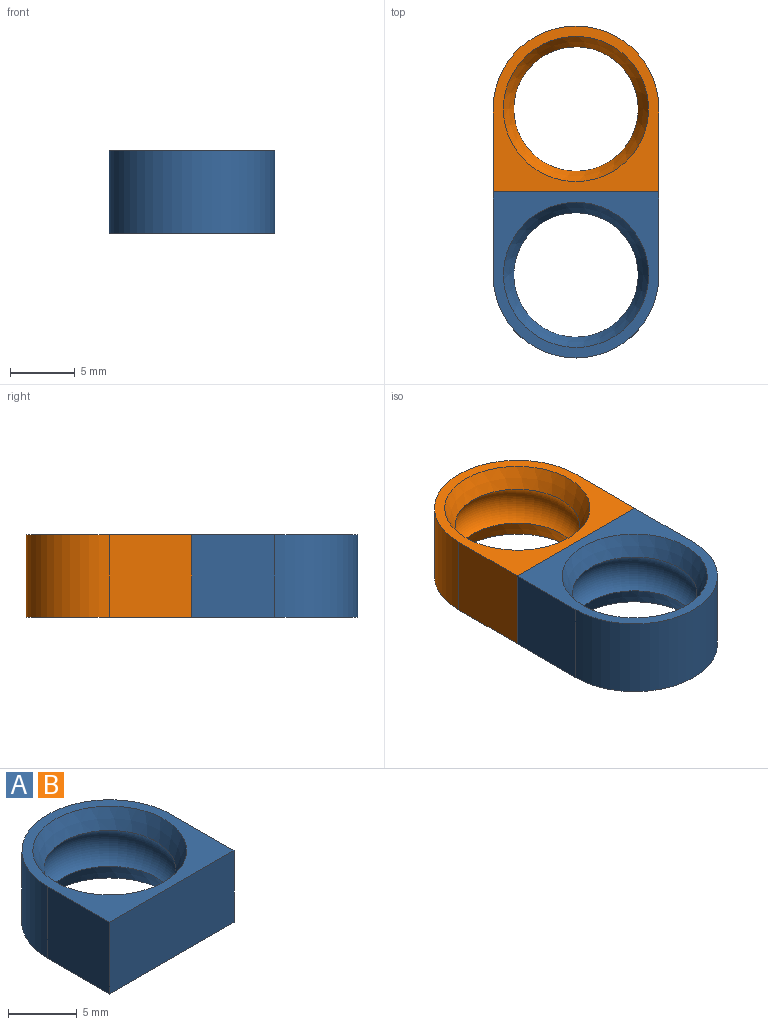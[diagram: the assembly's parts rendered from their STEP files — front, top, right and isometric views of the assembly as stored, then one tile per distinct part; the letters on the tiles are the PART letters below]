
ASSEMBLY  parts=2 mates=1
PART A: 9 faces, bbox 12.8x12.8x6.4 mm
  f0: cylinder r=6.4mm len=12.8mm, axis (0,0,-1), area 128.7mm2, adj f1,f5,f6,f8
  f1: plane 12.8x12.8mm, normal (0,0,-1), area 47.7mm2, adj f0,f2,f6,f7,f8
  f2: cone r=5.6mm half-angle=26.6deg, axis (0,0,-1), area 58.4mm2, adj f1,f3
  f3: torus R=3.6mm, axis (0,0,-1), area 124.1mm2, adj f2,f4
  f4: cone r=5.6mm half-angle=26.6deg, axis (0,0,1), area 58.4mm2, adj f3,f5
  f5: plane 12.8x12.8mm, normal (0,0,1), area 47.7mm2, adj f0,f4,f6,f7,f8
  f6: plane 6.4x6.4mm, normal (-1,0,0), area 41mm2, adj f0,f1,f5,f7
  f7: plane 12.8x6.4mm, normal (0,-1,0), area 81.9mm2, adj f1,f5,f6,f8
  f8: plane 6.4x6.4mm, normal (1,0,0), area 41mm2, adj f0,f1,f5,f7
PART B: same geometry as A
PLACE A rot(axis=(0,0,1),180deg) t=(19.85,48.89,4.95)mm
PLACE B t=(19.85,-2.31,4.95)mm
MATE fastened B.f7 <-> A.f7  axis (0,-1,0) through (19.85,23.29,8.15)mm
